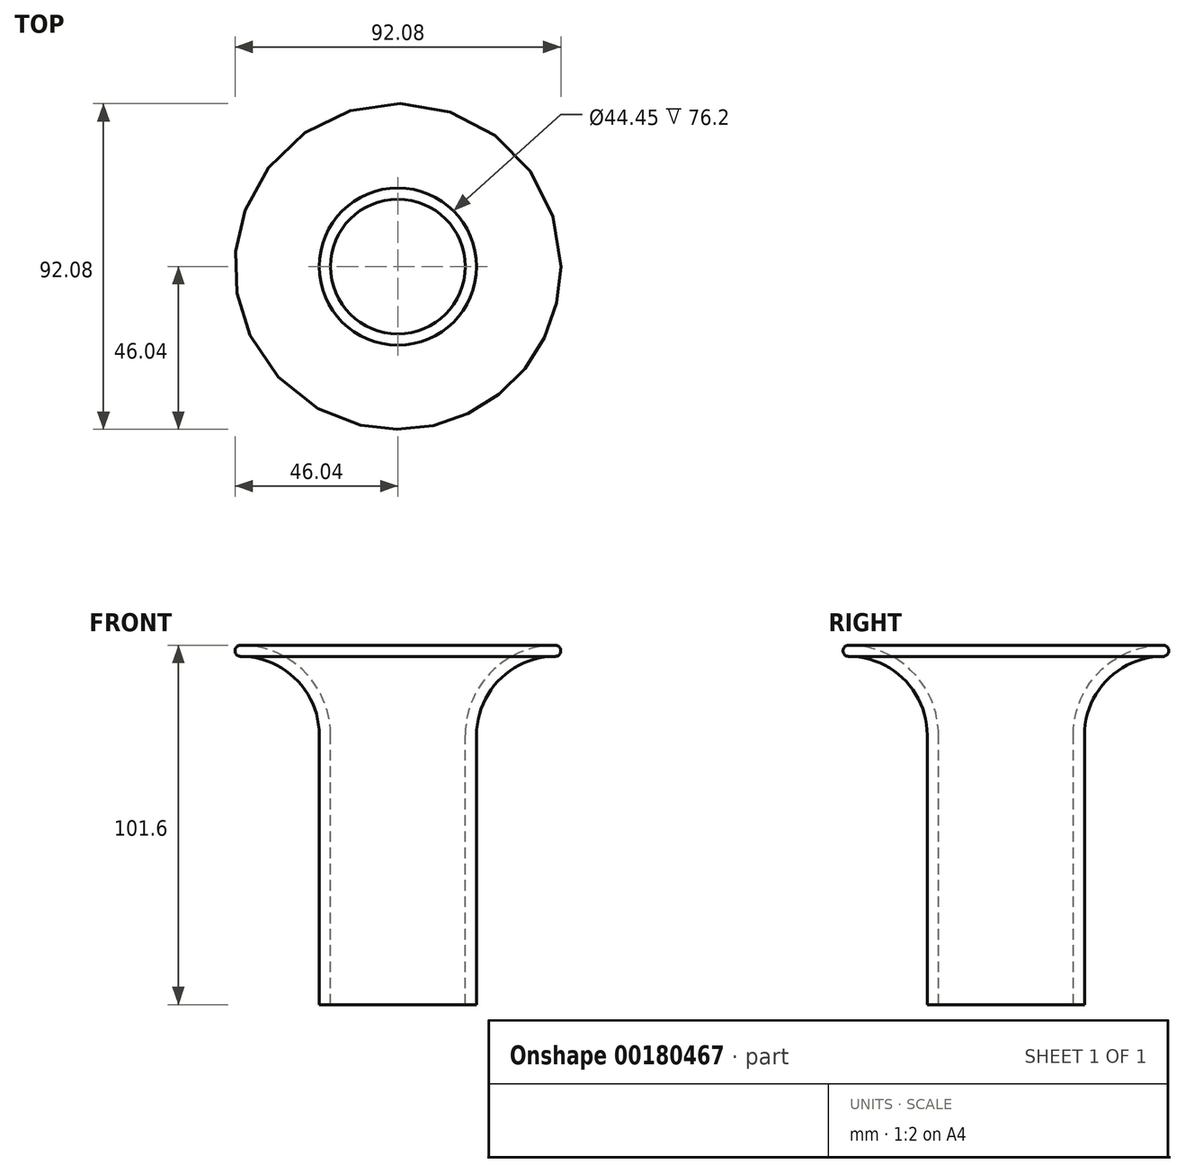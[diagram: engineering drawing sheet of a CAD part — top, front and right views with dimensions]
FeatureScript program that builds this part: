
annotation { "Feature Type Name" : "Feature", "Feature Type Description" : "" }
export const myFeature = defineFeature(function(context is Context, id is Id, definition is map)
    precondition{}
    {
        {
            var Q0;
            Q0=qCreatedBy(makeId("Right.planeOp"),FACE);
            var sketch = newSketch(context, id + "F0", { "sketchPlane" : qUnion([Q0])});
            skLineSegment(sketch, "E0", {"start": v(0, 0) * mm, "end": v(0, 76.2) * mm});
            skLineSegment(sketch, "E1", {"start": v(25.4, 101.6) * mm, "end": v(25.4, 101.6) * mm});
            skPoint(sketch, "E2.visualSharp", {"position": v(0, 101.6) * mm});
            skArc(sketch, "E2.filletArc", {"start": v(25.4, 101.6) * mm, "mid": v(7.44, 94.16) * mm, "end": v(0, 76.2) * mm});
            skLineSegment(sketch, "E3", {"start": v(0, 0) * mm, "end": v(-19.05, 0) * mm});
            skLineSegment(sketch, "E4", {"start": v(-19.05, 0) * mm, "end": v(-19.05, 50.8) * mm});
            skLineSegment(sketch, "E5.0", {"start": v(3.18, 0) * mm, "end": v(3.18, 76.2) * mm});
            skArc(sketch, "E5.1", {"start": v(25.4, 98.43) * mm, "mid": v(9.68, 91.92) * mm, "end": v(3.17, 76.2) * mm});
            skArc(sketch, "E6", {"start": v(25.4, 98.43) * mm, "mid": v(26.99, 100.01) * mm, "end": v(25.4, 101.6) * mm});
            skLineSegment(sketch, "E7", {"start": v(0, 0) * mm, "end": v(3.18, 0) * mm});
            skSolve(sketch);
        }
        {
            var Q0;
            Q0=sQuery(id+"F0.wireOp",EDGE,"E2.filletArc");
            var Q1;
            Q1=sQuery(id+"F0.wireOp",EDGE,"E0");
            var Q2;
            Q2=sQuery(id+"F0.wireOp",EDGE,"E5.0");
            var Q3;
            Q3=sQuery(id+"F0.wireOp",EDGE,"E7");
            var Q4;
            Q4=sQuery(id+"F0.wireOp",EDGE,"E5.1");
            var Q5;
            Q5=sQuery(id+"F0.wireOp",EDGE,"E6");
            var Q6;
            Q6=sQuery(id+"F0.wireOp",EDGE,"E4");
            revolve(context, id + "F1", {"bodyType" : ToolBodyType.SURFACE, "surfaceEntities" : qUnion([Q0, Q1, Q2, Q3, Q4, Q5]), "axis" : qUnion([Q6]), "revolveType" : RevolveType.FULL});
        }
    });
